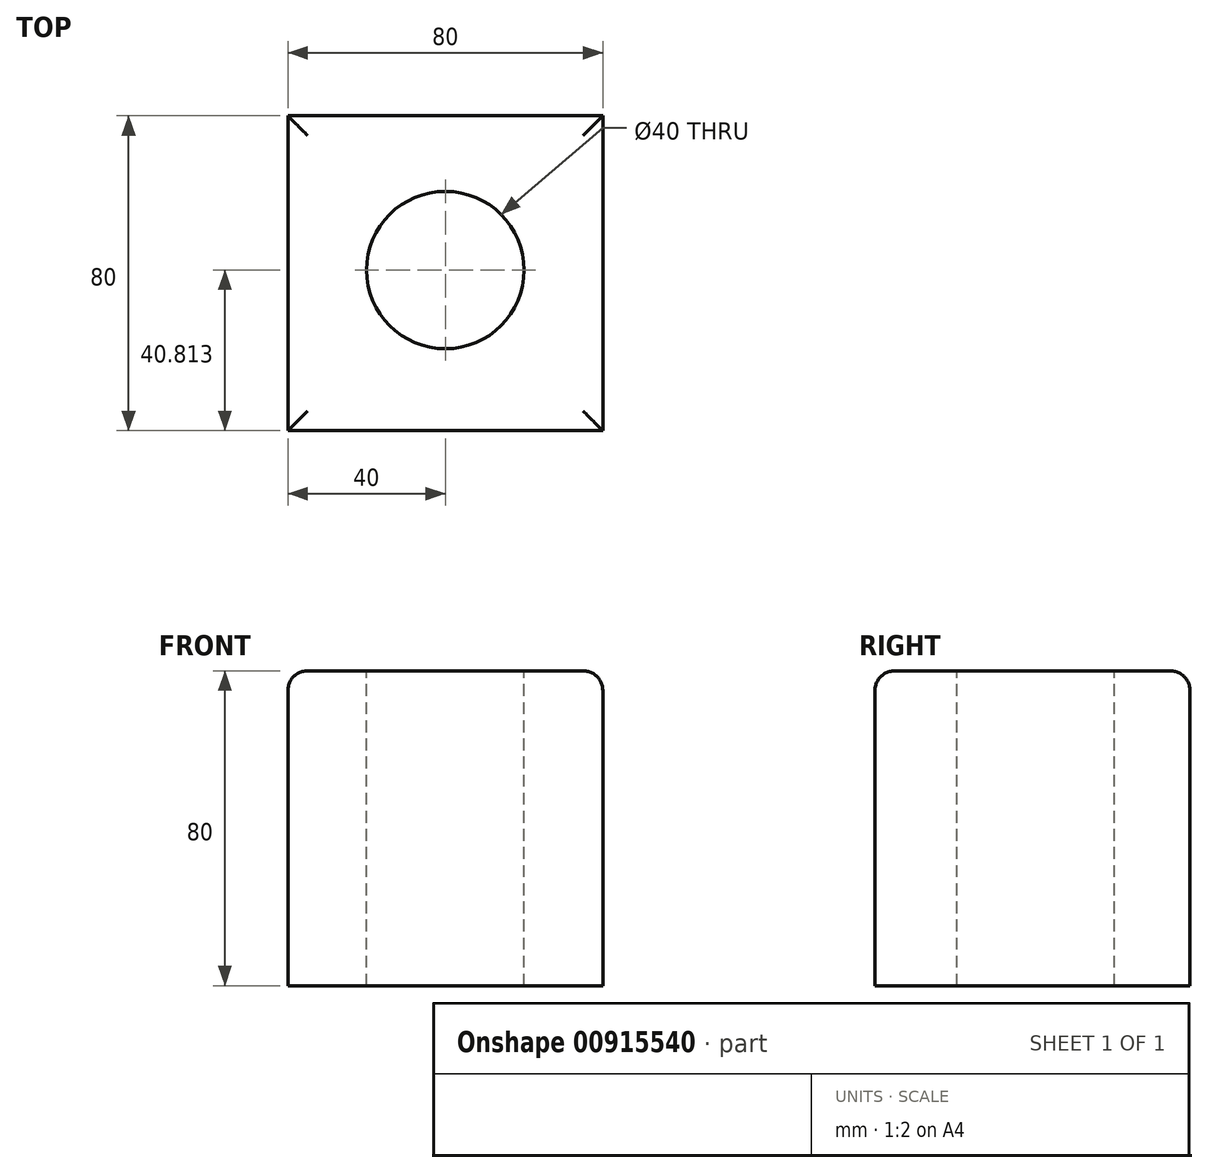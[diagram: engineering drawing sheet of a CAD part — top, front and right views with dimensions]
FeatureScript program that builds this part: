
annotation { "Feature Type Name" : "Feature", "Feature Type Description" : "" }
export const myFeature = defineFeature(function(context is Context, id is Id, definition is map)
    precondition{}
    {
        {
            var Q0;
            Q0=qCreatedBy(makeId("Front.planeOp"),FACE);
            var sketch = newSketch(context, id + "F0", { "sketchPlane" : qUnion([Q0])});
            skLineSegment(sketch, "E0.bottom", {"start": v(-40, -40) * mm, "end": v(40, -40) * mm});
            skLineSegment(sketch, "E0.top", {"start": v(-40, 40) * mm, "end": v(40, 40) * mm});
            skLineSegment(sketch, "E0.left", {"start": v(-40, -40) * mm, "end": v(-40, 40) * mm});
            skLineSegment(sketch, "E0.right", {"start": v(40, -40) * mm, "end": v(40, 40) * mm});
            skLineSegment(sketch, "E1", {"start": v(0, 0) * mm, "end": v(0, 40) * mm, "construction": true});
            skLineSegment(sketch, "E2", {"start": v(0, 0) * mm, "end": v(-40, 0) * mm, "construction": true});
            skSolve(sketch);
        }
        {
            var Q0;
            Q0 = qSketchRegion(id + "F0", true);
            extrude(context, id + "F1", {"entities" : qUnion([Q0]), "endBound" : BoundingType.SYMMETRIC, "depth" : 80 * mm, "offsetDistance" : 25 * mm});
        }
        {
            var Q0;
            Q0=makeQuery(id+"F1.opExtrude","SWEPT_FACE",FACE,{"disambiguationData":[OSD([sQuery(id+"F0.wireOp",EDGE,"E0.top")])]});
            var sketch = newSketch(context, id + "F2", { "sketchPlane" : qUnion([Q0])});
            skCircle(sketch, "E3", {"center": v(0, 0.81) * mm, "radius": 20 * mm});
            skSolve(sketch);
        }
        {
            var Q0;
            Q0 = qSketchRegion(id + "F2", true);
            extrude(context, id + "F3", {"entities" : qUnion([Q0]), "operationType" : NewBodyOperationType.REMOVE, "endBound" : BoundingType.THROUGH_ALL, "oppositeDirection" : true, "depth" : 25 * mm, "offsetDistance" : 25 * mm});
        }
        {
            var Q0;
            Q0=makeQuery(id+"F1.opExtrude","SWEPT_EDGE",EDGE,{"disambiguationData":[OSD([sQuery(id+"F0.wireOp",EDGE,"E0.top"),sQuery(id+"F0.wireOp",EDGE,"E0.left")])]});
            var Q1;
            Q1=makeQuery(id+"F1.opExtrude","CAP_EDGE",EDGE,{"disambiguationData":[OSD([sQuery(id+"F0.wireOp",EDGE,"E0.top")])],"isStart":false});
            var Q2;
            Q2=makeQuery(id+"F1.opExtrude","SWEPT_EDGE",EDGE,{"disambiguationData":[OSD([sQuery(id+"F0.wireOp",EDGE,"E0.top"),sQuery(id+"F0.wireOp",EDGE,"E0.right")])]});
            var Q3;
            Q3=makeQuery(id+"F1.opExtrude","CAP_EDGE",EDGE,{"disambiguationData":[OSD([sQuery(id+"F0.wireOp",EDGE,"E0.top")])],"isStart":true});
            fillet(context, id + "F4", {"entities" : qUnion([Q0, Q1, Q2, Q3]), "radius" : 5 * mm, "tangentPropagation" : true, "allowEdgeOverflow" : false});
        }
    });
